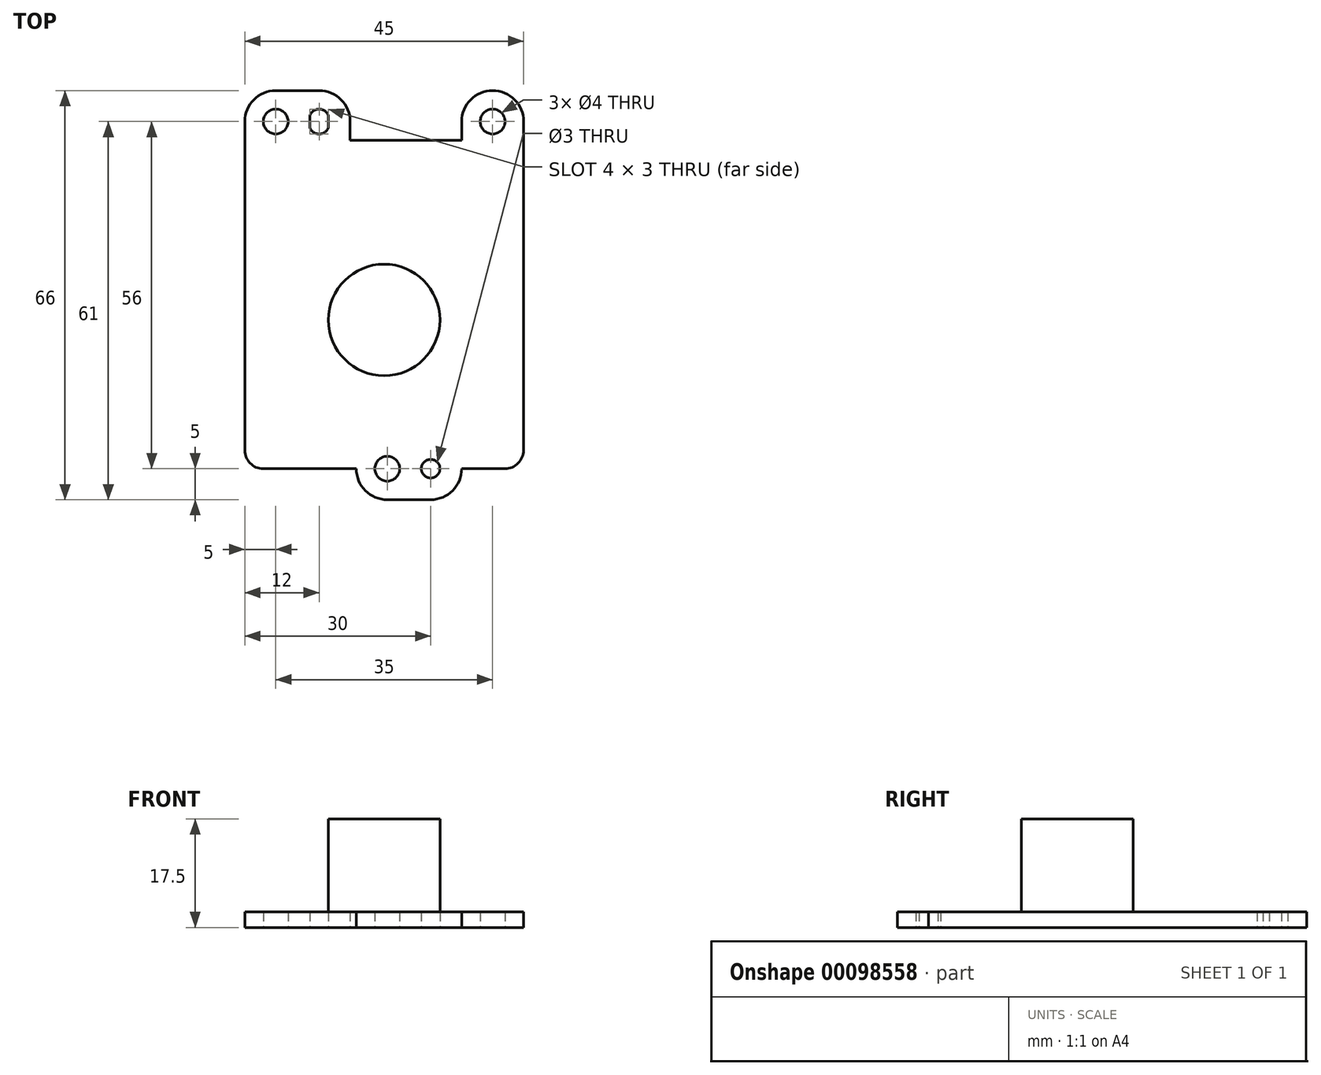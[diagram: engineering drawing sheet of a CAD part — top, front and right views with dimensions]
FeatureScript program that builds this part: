
annotation { "Feature Type Name" : "Feature", "Feature Type Description" : "" }
export const myFeature = defineFeature(function(context is Context, id is Id, definition is map)
    precondition{}
    {
        {
            var Q0;
            Q0=qCreatedBy(makeId("Top.planeOp"),FACE);
            var sketch = newSketch(context, id + "F0", { "sketchPlane" : qUnion([Q0])});
            skLineSegment(sketch, "E0.bottom", {"start": v(22.5, -25) * mm, "end": v(-22.5, -25) * mm, "construction": true});
            skLineSegment(sketch, "E0.top", {"start": v(22.5, 25) * mm, "end": v(-22.5, 25) * mm, "construction": true});
            skLineSegment(sketch, "E0.left", {"start": v(22.5, -25) * mm, "end": v(22.5, 25) * mm});
            skLineSegment(sketch, "E0.right", {"start": v(-22.5, -25) * mm, "end": v(-22.5, 25) * mm});
            skPoint(sketch, "E0.middle", {"position": v(0, 0) * mm});
            skCircle(sketch, "E1", {"center": v(17.5, 28) * mm, "radius": 2 * mm});
            skCircle(sketch, "E2", {"center": v(-17.5, 28) * mm, "radius": 2 * mm});
            skLineSegment(sketch, "E3", {"start": v(-12, 29) * mm, "end": v(-12, 27) * mm});
            skLineSegment(sketch, "E4", {"start": v(-9, 29) * mm, "end": v(-9, 27) * mm});
            skLineSegment(sketch, "E5", {"start": v(-12, 29) * mm, "end": v(-9, 29) * mm, "construction": true});
            skLineSegment(sketch, "E6", {"start": v(-12, 27) * mm, "end": v(-9, 27) * mm, "construction": true});
            skArc(sketch, "E7", {"start": v(-9, 29) * mm, "mid": v(-10.5, 30) * mm, "end": v(-12, 29) * mm});
            skArc(sketch, "E8", {"start": v(-12, 27) * mm, "mid": v(-10.5, 26) * mm, "end": v(-9, 27) * mm});
            skLineSegment(sketch, "E9", {"start": v(-10.5, 30) * mm, "end": v(-10.5, 26) * mm, "construction": true});
            skLineSegment(sketch, "E10", {"start": v(-22.5, 25) * mm, "end": v(-22.5, 28) * mm});
            skLineSegment(sketch, "E11", {"start": v(-22.5, 28) * mm, "end": v(22.5, 28) * mm, "construction": true});
            skLineSegment(sketch, "E12", {"start": v(22.5, 28) * mm, "end": v(22.5, 25) * mm});
            skPoint(sketch, "E13", {"position": v(-10.5, 28) * mm});
            skLineSegment(sketch, "E14", {"start": v(-17.5, 33) * mm, "end": v(-10.5, 33) * mm});
            skLineSegment(sketch, "E15", {"start": v(-10.5, 33) * mm, "end": v(-10.5, 28) * mm, "construction": true});
            skLineSegment(sketch, "E16", {"start": v(-17.5, 33) * mm, "end": v(-17.5, 28) * mm, "construction": true});
            skArc(sketch, "E17", {"start": v(-22.5, 28) * mm, "mid": v(-21.04, 31.54) * mm, "end": v(-17.5, 33) * mm});
            skArc(sketch, "E18", {"start": v(-10.5, 33) * mm, "mid": v(-6.96, 31.54) * mm, "end": v(-5.5, 28) * mm});
            skLineSegment(sketch, "E19", {"start": v(-5.5, 28) * mm, "end": v(-5.5, 25) * mm});
            skLineSegment(sketch, "E20", {"start": v(-5.5, 25) * mm, "end": v(12.5, 25) * mm});
            skLineSegment(sketch, "E21", {"start": v(12.5, 25) * mm, "end": v(12.5, 28) * mm});
            skArc(sketch, "E22", {"start": v(12.5, 28) * mm, "mid": v(17.5, 33) * mm, "end": v(22.5, 28) * mm});
            skCircle(sketch, "E23", {"center": v(7.5, -28) * mm, "radius": 1.5 * mm});
            skCircle(sketch, "E24", {"center": v(0.5, -28) * mm, "radius": 2 * mm});
            skLineSegment(sketch, "E25", {"start": v(0.5, -28) * mm, "end": v(0.5, -33) * mm, "construction": true});
            skLineSegment(sketch, "E26", {"start": v(0.5, -33) * mm, "end": v(7.5, -33) * mm});
            skLineSegment(sketch, "E27", {"start": v(7.5, -33) * mm, "end": v(7.5, -28) * mm, "construction": true});
            skLineSegment(sketch, "E28", {"start": v(-19.5, -28) * mm, "end": v(19.5, -28) * mm, "construction": true});
            skArc(sketch, "E29", {"start": v(7.5, -33) * mm, "mid": v(11.04, -31.54) * mm, "end": v(12.5, -28) * mm});
            skArc(sketch, "E30", {"start": v(0.5, -33) * mm, "mid": v(-3.04, -31.54) * mm, "end": v(-4.5, -28) * mm});
            skArc(sketch, "E31", {"start": v(-22.5, -25) * mm, "mid": v(-21.62, -27.12) * mm, "end": v(-19.5, -28) * mm});
            skArc(sketch, "E32", {"start": v(22.5, -25) * mm, "mid": v(21.62, -27.12) * mm, "end": v(19.5, -28) * mm});
            skLineSegment(sketch, "E33", {"start": v(-19.5, -25) * mm, "end": v(-19.5, -28) * mm});
            skLineSegment(sketch, "E34", {"start": v(19.5, -25) * mm, "end": v(19.5, -28) * mm});
            skLineSegment(sketch, "E35", {"start": v(12.5, -28) * mm, "end": v(19.5, -28) * mm});
            skLineSegment(sketch, "E36", {"start": v(-19.5, -28) * mm, "end": v(-4.5, -28) * mm});
            skSolve(sketch);
        }
        {
            var Q0;
            Q0=makeQuery(id+"F0.imprint","IMPRINT",FACE,{"disambiguationData":[TD([[makeQuery(id+"F0.imprint","IMPRINT",EDGE,{"derivedFrom":sQuery(id+"F0.wireOp",EDGE,"E0.left")}),1.0]])]});
            extrude(context, id + "F1", {"entities" : qUnion([Q0]), "depth" : 2.5 * mm});
        }
        {
            var Q0;
            Q0=makeQuery(id+"F1.opExtrude","CAP_FACE",FACE,{"disambiguationData":[OSD([sQuery(id+"F0.wireOp",EDGE,"E0.left"),sQuery(id+"F0.wireOp",EDGE,"E0.right"),sQuery(id+"F0.wireOp",EDGE,"E1"),sQuery(id+"F0.wireOp",EDGE,"E2"),sQuery(id+"F0.wireOp",EDGE,"E3"),sQuery(id+"F0.wireOp",EDGE,"E4"),sQuery(id+"F0.wireOp",EDGE,"E7"),sQuery(id+"F0.wireOp",EDGE,"E8"),sQuery(id+"F0.wireOp",EDGE,"E10"),sQuery(id+"F0.wireOp",EDGE,"E12"),sQuery(id+"F0.wireOp",EDGE,"E14"),sQuery(id+"F0.wireOp",EDGE,"E17"),sQuery(id+"F0.wireOp",EDGE,"E18"),sQuery(id+"F0.wireOp",EDGE,"E19"),sQuery(id+"F0.wireOp",EDGE,"E20"),sQuery(id+"F0.wireOp",EDGE,"E21"),sQuery(id+"F0.wireOp",EDGE,"E22"),sQuery(id+"F0.wireOp",EDGE,"E23"),sQuery(id+"F0.wireOp",EDGE,"E24"),sQuery(id+"F0.wireOp",EDGE,"E26"),sQuery(id+"F0.wireOp",EDGE,"E29"),sQuery(id+"F0.wireOp",EDGE,"E30"),sQuery(id+"F0.wireOp",EDGE,"E31"),sQuery(id+"F0.wireOp",EDGE,"E32"),sQuery(id+"F0.wireOp",EDGE,"E35"),sQuery(id+"F0.wireOp",EDGE,"E36")])],"isStart":false});
            var sketch = newSketch(context, id + "F2", { "sketchPlane" : qUnion([Q0])});
            skCircle(sketch, "E37", {"center": v(0, -4) * mm, "radius": 9 * mm});
            skSolve(sketch);
        }
        {
            var Q0;
            Q0 = qSketchRegion(id + "F2", true);
            extrude(context, id + "F3", {"entities" : qUnion([Q0]), "operationType" : NewBodyOperationType.ADD, "depth" : 15 * mm});
        }
    });
